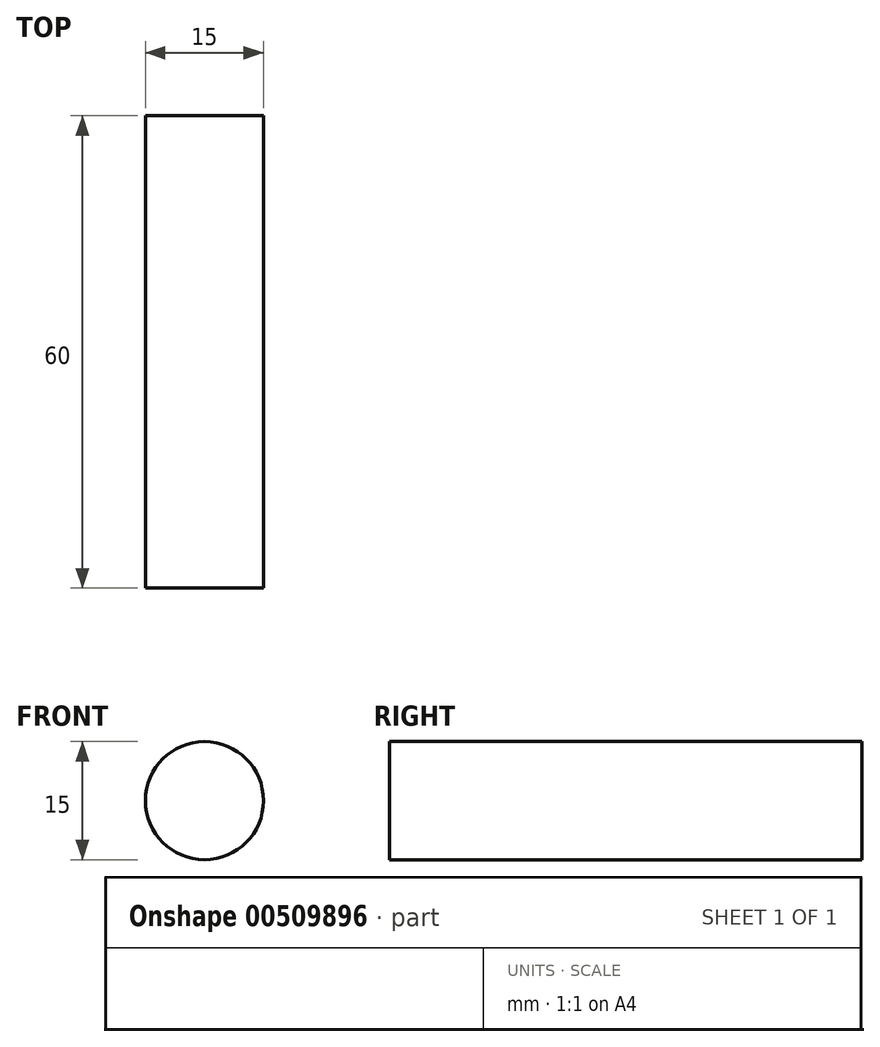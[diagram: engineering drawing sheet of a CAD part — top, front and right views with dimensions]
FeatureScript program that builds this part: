
annotation { "Feature Type Name" : "Feature", "Feature Type Description" : "" }
export const myFeature = defineFeature(function(context is Context, id is Id, definition is map)
    precondition{}
    {
        {
            var Q0;
            Q0=qCreatedBy(makeId("Front.planeOp"),FACE);
            var sketch = newSketch(context, id + "F0", { "sketchPlane" : qUnion([Q0])});
            skCircle(sketch, "E0", {"center": v(0, 0) * mm, "radius": 7.5 * mm});
            skSolve(sketch);
        }
        {
            var Q0;
            Q0=makeQuery(id+"F0.imprint","IMPRINT",FACE,{"disambiguationData":[TD([[makeQuery(id+"F0.imprint","IMPRINT",EDGE,{"derivedFrom":sQuery(id+"F0.wireOp",EDGE,"E0")}),1.0]])]});
            extrude(context, id + "F1", {"entities" : qUnion([Q0]), "depth" : 60 * mm, "offsetDistance" : 25 * mm});
        }
    });
